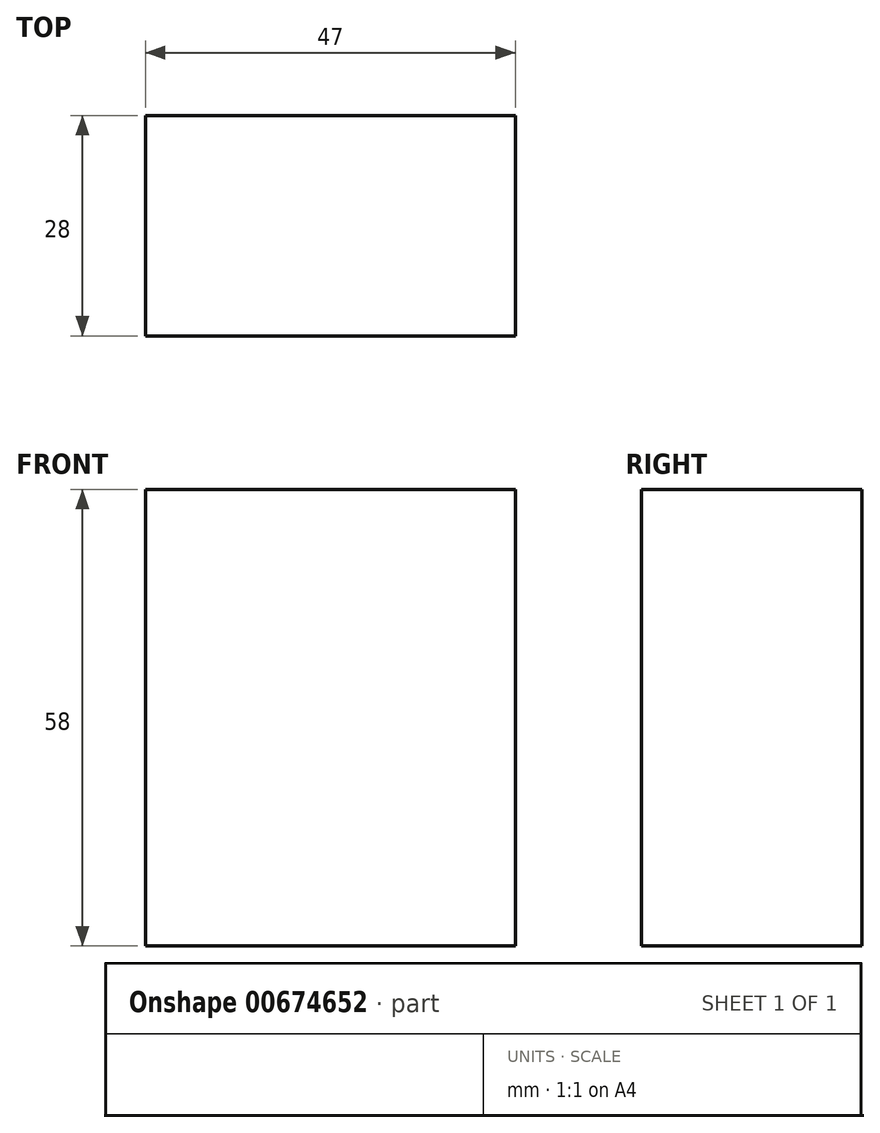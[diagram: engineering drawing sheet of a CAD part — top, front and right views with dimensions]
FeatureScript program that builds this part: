
annotation { "Feature Type Name" : "Feature", "Feature Type Description" : "" }
export const myFeature = defineFeature(function(context is Context, id is Id, definition is map)
    precondition{}
    {
        {
            var Q0;
            Q0=qCreatedBy(makeId("Front.planeOp"),FACE);
            var sketch = newSketch(context, id + "F0", { "sketchPlane" : qUnion([Q0])});
            skLineSegment(sketch, "E0.bottom", {"start": v(0, 0) * mm, "end": v(47, 0) * mm});
            skLineSegment(sketch, "E0.top", {"start": v(0, 58) * mm, "end": v(47, 58) * mm});
            skLineSegment(sketch, "E0.left", {"start": v(0, 0) * mm, "end": v(0, 58) * mm});
            skLineSegment(sketch, "E0.right", {"start": v(47, 0) * mm, "end": v(47, 58) * mm});
            skSolve(sketch);
        }
        {
            var Q0;
            Q0=makeQuery(id+"F0.imprint","IMPRINT",FACE,{"disambiguationData":[TD([[makeQuery(id+"F0.imprint","IMPRINT",EDGE,{"derivedFrom":sQuery(id+"F0.wireOp",EDGE,"E0.bottom")}),1.0]])]});
            extrude(context, id + "F1", {"entities" : qUnion([Q0]), "depth" : 28 * mm, "offsetDistance" : 25.4 * mm});
        }
    });
